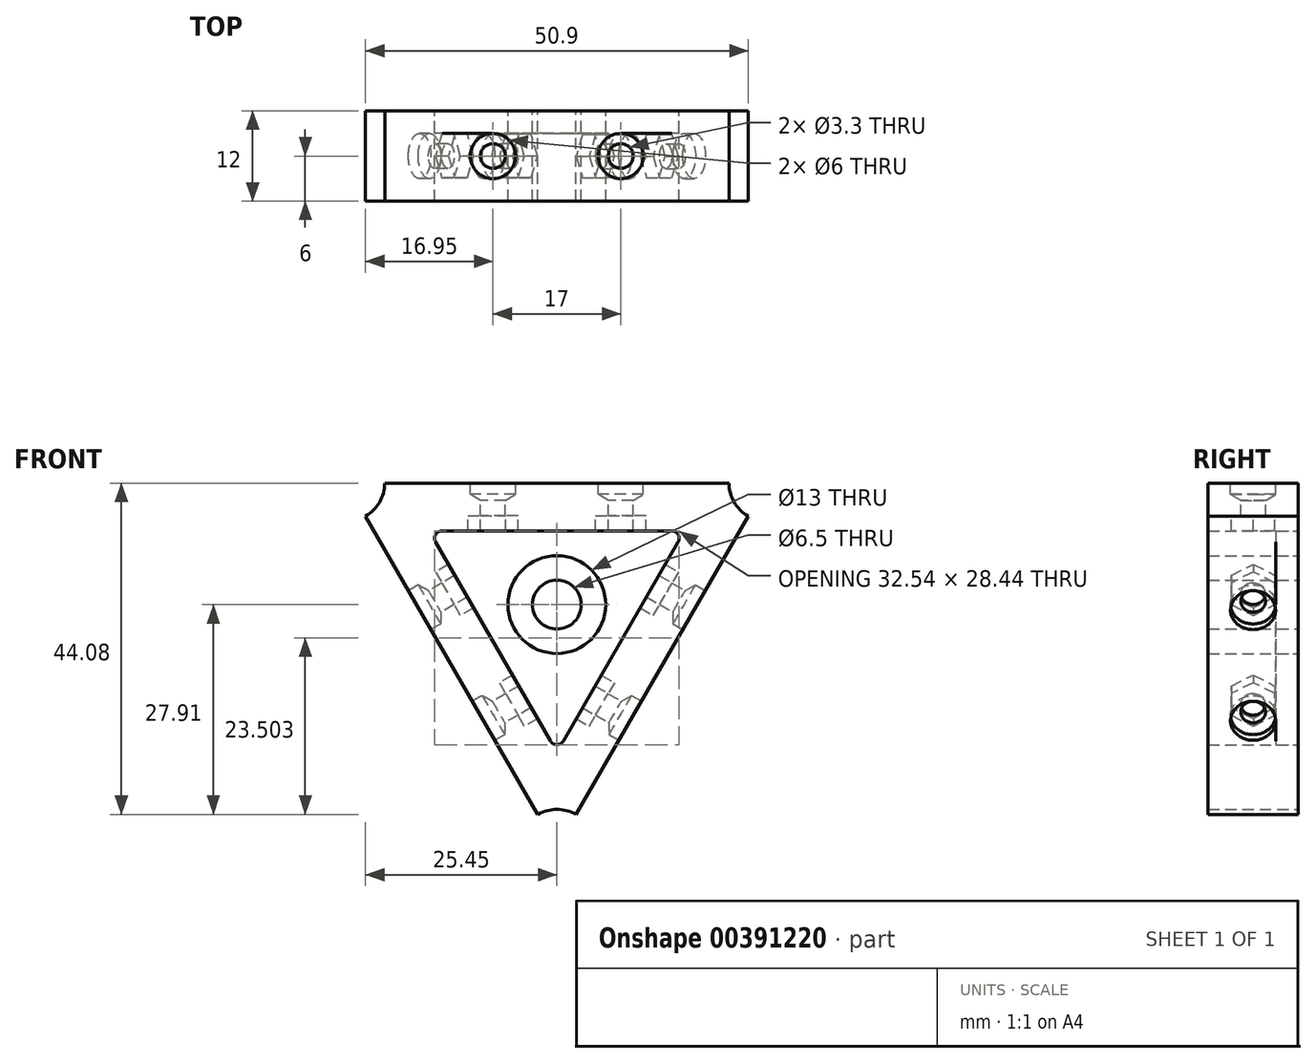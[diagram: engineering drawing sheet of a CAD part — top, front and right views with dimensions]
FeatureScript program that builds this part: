
annotation { "Feature Type Name" : "Feature", "Feature Type Description" : "" }
export const myFeature = defineFeature(function(context is Context, id is Id, definition is map)
    precondition{}
    {
        {
            var Q0;
            Q0=qCreatedBy(makeId("Front.planeOp"),FACE);
            var sketch = newSketch(context, id + "F0", { "sketchPlane" : qUnion([Q0])});
            skCircle(sketch, "E0.cCircle", {"center": v(0, 0) * mm, "radius": 9.81 * mm, "construction": true});
            skLineSegment(sketch, "E0.0", {"start": v(16.13, 8.31) * mm, "end": v(0.87, -18.13) * mm});
            skLineSegment(sketch, "E0.1", {"start": v(-0.87, -18.13) * mm, "end": v(-16.13, 8.31) * mm});
            skLineSegment(sketch, "E0.2", {"start": v(-15.27, 9.81) * mm, "end": v(15.27, 9.81) * mm});
            skPoint(sketch, "E0.0.midPoint", {"position": v(8.5, -4.9) * mm});
            skPoint(sketch, "E1.0.midPoint", {"position": v(14, -8.08) * mm});
            skPoint(sketch, "E2", {"position": v(0, 9.81) * mm});
            skCircle(sketch, "E3", {"center": v(0, 0) * mm, "radius": 3.25 * mm});
            skPoint(sketch, "E4", {"position": v(22.9, 16.17) * mm});
            skPoint(sketch, "E5", {"position": v(-22.9, 16.17) * mm});
            skPoint(sketch, "E6", {"position": v(-25.45, 11.75) * mm});
            skPoint(sketch, "E7", {"position": v(-2.55, -27.91) * mm});
            skPoint(sketch, "E8", {"position": v(2.55, -27.91) * mm});
            skPoint(sketch, "E9", {"position": v(25.45, 11.75) * mm});
            skCircle(sketch, "E10", {"center": v(28, 16.17) * mm, "radius": 5.1 * mm});
            skCircle(sketch, "E11", {"center": v(0, -32.33) * mm, "radius": 5.1 * mm});
            skCircle(sketch, "E12", {"center": v(-28, 16.17) * mm, "radius": 5.1 * mm});
            skLineSegment(sketch, "E13", {"start": v(-22.9, 16.17) * mm, "end": v(22.9, 16.17) * mm});
            skLineSegment(sketch, "E14", {"start": v(25.45, 11.75) * mm, "end": v(2.55, -27.91) * mm});
            skLineSegment(sketch, "E15", {"start": v(-25.45, 11.75) * mm, "end": v(-2.55, -27.91) * mm});
            skPoint(sketch, "E16.visualSharp", {"position": v(17, 9.81) * mm});
            skArc(sketch, "E16.filletArc", {"start": v(16.13, 8.31) * mm, "mid": v(16.13, 9.31) * mm, "end": v(15.27, 9.81) * mm});
            skPoint(sketch, "E17.visualSharp", {"position": v(-17, 9.81) * mm});
            skArc(sketch, "E17.filletArc", {"start": v(-15.27, 9.81) * mm, "mid": v(-16.13, 9.31) * mm, "end": v(-16.13, 8.31) * mm});
            skPoint(sketch, "E18.visualSharp", {"position": v(0, -19.63) * mm});
            skArc(sketch, "E18.filletArc", {"start": v(-0.87, -18.13) * mm, "mid": v(0, -18.63) * mm, "end": v(0.87, -18.13) * mm});
            skCircle(sketch, "E19", {"center": v(0, 0) * mm, "radius": 6.5 * mm});
            skSolve(sketch);
        }
        {
            var Q0;
            Q0=makeQuery(id+"F0.imprint","IMPRINT",FACE,{"disambiguationData":[TD([[makeQuery(id+"F0.imprint","IMPRINT",EDGE,{"derivedFrom":sQuery(id+"F0.wireOp",EDGE,"E0.0")}),1.0]])]});
            var Q1;
            Q1=makeQuery(id+"F0.imprint","IMPRINT",FACE,{"disambiguationData":[TD([[makeQuery(id+"F0.imprint","IMPRINT",EDGE,{"derivedFrom":sQuery(id+"F0.wireOp",EDGE,"E3")}),-1.0]])]});
            extrude(context, id + "F1", {"entities" : qUnion([Q0, Q1]), "depth" : 12 * mm});
        }
        {
            var Q0;
            Q0=makeQuery(id+"F0.imprint","IMPRINT",FACE,{"disambiguationData":[TD([[makeQuery(id+"F0.imprint","IMPRINT",EDGE,{"derivedFrom":sQuery(id+"F0.wireOp",EDGE,"E0.0")}),-1.0]])]});
            extrude(context, id + "F2", {"entities" : qUnion([Q0]), "depth" : 3 * mm});
        }
        {
            var Q0;
            Q0=makeQuery(id+"F1.opExtrude","SWEPT_FACE",FACE,{"disambiguationData":[OSD([sQuery(id+"F0.wireOp",EDGE,"E13")])]});
            var sketch = newSketch(context, id + "F3", { "sketchPlane" : qUnion([Q0])});
            skPoint(sketch, "E20", {"position": v(8.5, -6) * mm});
            skPoint(sketch, "E21", {"position": v(-8.5, -6) * mm});
            skCircle(sketch, "E22.cCircle", {"center": v(-8.5, -6) * mm, "radius": 2.9 * mm, "construction": true});
            skLineSegment(sketch, "E22.0", {"start": v(-5.15, -6) * mm, "end": v(-6.83, -8.9) * mm});
            skLineSegment(sketch, "E22.1", {"start": v(-6.83, -8.9) * mm, "end": v(-10.17, -8.9) * mm});
            skLineSegment(sketch, "E22.2", {"start": v(-10.17, -8.9) * mm, "end": v(-11.85, -6) * mm});
            skLineSegment(sketch, "E22.3", {"start": v(-11.85, -6) * mm, "end": v(-10.17, -3.1) * mm});
            skLineSegment(sketch, "E22.4", {"start": v(-10.17, -3.1) * mm, "end": v(-6.83, -3.1) * mm});
            skLineSegment(sketch, "E22.5", {"start": v(-6.83, -3.1) * mm, "end": v(-5.15, -6) * mm});
            skPoint(sketch, "E22.0.midPoint", {"position": v(-5.99, -7.45) * mm});
            skCircle(sketch, "E23.cCircle", {"center": v(8.5, -6) * mm, "radius": 2.9 * mm, "construction": true});
            skLineSegment(sketch, "E23.0", {"start": v(11.85, -6) * mm, "end": v(10.17, -8.9) * mm});
            skLineSegment(sketch, "E23.1", {"start": v(10.17, -8.9) * mm, "end": v(6.83, -8.9) * mm});
            skLineSegment(sketch, "E23.2", {"start": v(6.83, -8.9) * mm, "end": v(5.15, -6) * mm});
            skLineSegment(sketch, "E23.3", {"start": v(5.15, -6) * mm, "end": v(6.83, -3.1) * mm});
            skLineSegment(sketch, "E23.4", {"start": v(6.83, -3.1) * mm, "end": v(10.17, -3.1) * mm});
            skLineSegment(sketch, "E23.5", {"start": v(10.17, -3.1) * mm, "end": v(11.85, -6) * mm});
            skPoint(sketch, "E23.0.midPoint", {"position": v(11.01, -7.45) * mm});
            skSolve(sketch);
        }
        {
            var Q0;
            Q0 = qSketchRegion(id + "F3", true);
            extrude(context, id + "F4", {"entities" : qUnion([Q0]), "operationType" : NewBodyOperationType.REMOVE, "oppositeDirection" : true, "depth" : 8 * mm, "hasSecondDirection" : true, "secondDirectionOppositeDirection" : true, "secondDirectionDepth" : 4.35 * mm});
        }
        {
            var Q0;
            Q0=sQuery(id+"F3.wireOp",VERTEX,"E20");
            var Q1;
            Q1=sQuery(id+"F3.wireOp",VERTEX,"E21");
            var Q2;
            Q2=makeQuery(id+"F1.opExtrude","SWEPT_BODY",BODY,{"disambiguationData":[OSD([sQuery(id+"F0.wireOp",EDGE,"E0.0"),sQuery(id+"F0.wireOp",EDGE,"E0.1"),sQuery(id+"F0.wireOp",EDGE,"E0.2"),sQuery(id+"F0.wireOp",EDGE,"E10"),sQuery(id+"F0.wireOp",EDGE,"E11"),sQuery(id+"F0.wireOp",EDGE,"E12"),sQuery(id+"F0.wireOp",EDGE,"E13"),sQuery(id+"F0.wireOp",EDGE,"E14"),sQuery(id+"F0.wireOp",EDGE,"E15"),sQuery(id+"F0.wireOp",EDGE,"E16.filletArc"),sQuery(id+"F0.wireOp",EDGE,"E17.filletArc"),sQuery(id+"F0.wireOp",EDGE,"E18.filletArc")])]});
            hole(context, id + "F5", {"style" : HoleStyle.SIMPLE, "endStyle" : HoleEndStyle.BLIND, "standardTappedOrClearance" : lookupTablePath({ "standard" : "ISO", "fit" : "Normal", "size" : "M3", "type" : "Clearance" }), "standardBlindInLast" : lookupTablePath({ "fit" : "Standard", "standard" : "ISO", "size" : "M3", "type" : "Clearance" }), "holeDiameter" : 3.3 * mm, "holeDepth" : 8 * mm, "tappedDepth" : 12 * mm, "tapClearance" : 3, "locations" : qUnion([Q0, Q1]), "scope" : qUnion([Q2])});
        }
        {
            var Q0;
            Q0=sQuery(id+"F3.wireOp",VERTEX,"E20");
            var Q1;
            Q1=sQuery(id+"F3.wireOp",VERTEX,"E21");
            var Q2;
            Q2=makeQuery(id+"F1.opExtrude","SWEPT_BODY",BODY,{"disambiguationData":[OSD([sQuery(id+"F0.wireOp",EDGE,"E0.0"),sQuery(id+"F0.wireOp",EDGE,"E0.1"),sQuery(id+"F0.wireOp",EDGE,"E0.2"),sQuery(id+"F0.wireOp",EDGE,"E10"),sQuery(id+"F0.wireOp",EDGE,"E11"),sQuery(id+"F0.wireOp",EDGE,"E12"),sQuery(id+"F0.wireOp",EDGE,"E13"),sQuery(id+"F0.wireOp",EDGE,"E14"),sQuery(id+"F0.wireOp",EDGE,"E15"),sQuery(id+"F0.wireOp",EDGE,"E16.filletArc"),sQuery(id+"F0.wireOp",EDGE,"E17.filletArc"),sQuery(id+"F0.wireOp",EDGE,"E18.filletArc")])]});
            hole(context, id + "F6", {"style" : HoleStyle.SIMPLE, "endStyle" : HoleEndStyle.BLIND, "holeDiameter" : 6 * mm, "holeDepth" : 1.5 * mm, "tappedDepth" : 12 * mm, "tapClearance" : 3, "locations" : qUnion([Q0, Q1]), "scope" : qUnion([Q2])});
        }
        {
            var Q0;
            Q0=makeQuery(id+"F1.opExtrude","SWEPT_FACE",FACE,{"disambiguationData":[OSD([sQuery(id+"F0.wireOp",EDGE,"E15")])]});
            var sketch = newSketch(context, id + "F7", { "sketchPlane" : qUnion([Q0])});
            skPoint(sketch, "E24", {"position": v(6, -8.5) * mm});
            skPoint(sketch, "E25", {"position": v(6, 8.5) * mm});
            skCircle(sketch, "E26.cCircle", {"center": v(6, 8.5) * mm, "radius": 2.9 * mm, "construction": true});
            skLineSegment(sketch, "E26.0", {"start": v(6, 5.15) * mm, "end": v(3.1, 6.83) * mm});
            skLineSegment(sketch, "E26.1", {"start": v(3.1, 6.83) * mm, "end": v(3.1, 10.17) * mm});
            skLineSegment(sketch, "E26.2", {"start": v(3.1, 10.17) * mm, "end": v(6, 11.85) * mm});
            skLineSegment(sketch, "E26.3", {"start": v(6, 11.85) * mm, "end": v(8.9, 10.17) * mm});
            skLineSegment(sketch, "E26.4", {"start": v(8.9, 10.17) * mm, "end": v(8.9, 6.83) * mm});
            skLineSegment(sketch, "E26.5", {"start": v(8.9, 6.83) * mm, "end": v(6, 5.15) * mm});
            skPoint(sketch, "E26.0.midPoint", {"position": v(4.55, 5.99) * mm});
            skCircle(sketch, "E27.cCircle", {"center": v(6, -8.5) * mm, "radius": 2.9 * mm, "construction": true});
            skLineSegment(sketch, "E27.0", {"start": v(6, -11.85) * mm, "end": v(3.1, -10.17) * mm});
            skLineSegment(sketch, "E27.1", {"start": v(3.1, -10.17) * mm, "end": v(3.1, -6.83) * mm});
            skLineSegment(sketch, "E27.2", {"start": v(3.1, -6.83) * mm, "end": v(6, -5.15) * mm});
            skLineSegment(sketch, "E27.3", {"start": v(6, -5.15) * mm, "end": v(8.9, -6.83) * mm});
            skLineSegment(sketch, "E27.4", {"start": v(8.9, -6.83) * mm, "end": v(8.9, -10.17) * mm});
            skLineSegment(sketch, "E27.5", {"start": v(8.9, -10.17) * mm, "end": v(6, -11.85) * mm});
            skPoint(sketch, "E27.0.midPoint", {"position": v(4.55, -11.01) * mm});
            skSolve(sketch);
        }
        {
            var Q0;
            Q0=makeQuery(id+"F7.imprint","IMPRINT",FACE,{"disambiguationData":[TD([[makeQuery(id+"F7.imprint","IMPRINT",EDGE,{"derivedFrom":sQuery(id+"F7.wireOp",EDGE,"E26.0")}),-1.0]])]});
            var Q1;
            Q1=makeQuery(id+"F7.imprint","IMPRINT",FACE,{"disambiguationData":[TD([[makeQuery(id+"F7.imprint","IMPRINT",EDGE,{"derivedFrom":sQuery(id+"F7.wireOp",EDGE,"E27.0")}),-1.0]])]});
            extrude(context, id + "F8", {"entities" : qUnion([Q0, Q1]), "operationType" : NewBodyOperationType.REMOVE, "oppositeDirection" : true, "depth" : 8 * mm, "hasSecondDirection" : true, "secondDirectionOppositeDirection" : true, "secondDirectionDepth" : 4.35 * mm});
        }
        {
            var Q0;
            Q0=sQuery(id+"F7.wireOp",VERTEX,"E26.cCircle.center");
            var Q1;
            Q1=sQuery(id+"F7.wireOp",VERTEX,"E27.cCircle.center");
            var Q2;
            Q2=makeQuery(id+"F1.opExtrude","SWEPT_BODY",BODY,{"disambiguationData":[OSD([sQuery(id+"F0.wireOp",EDGE,"E0.0"),sQuery(id+"F0.wireOp",EDGE,"E0.1"),sQuery(id+"F0.wireOp",EDGE,"E0.2"),sQuery(id+"F0.wireOp",EDGE,"E10"),sQuery(id+"F0.wireOp",EDGE,"E11"),sQuery(id+"F0.wireOp",EDGE,"E12"),sQuery(id+"F0.wireOp",EDGE,"E13"),sQuery(id+"F0.wireOp",EDGE,"E14"),sQuery(id+"F0.wireOp",EDGE,"E15"),sQuery(id+"F0.wireOp",EDGE,"E16.filletArc"),sQuery(id+"F0.wireOp",EDGE,"E17.filletArc"),sQuery(id+"F0.wireOp",EDGE,"E18.filletArc")])]});
            hole(context, id + "F9", {"style" : HoleStyle.SIMPLE, "endStyle" : HoleEndStyle.BLIND, "holeDiameter" : 6 * mm, "holeDepth" : 1.5 * mm, "tappedDepth" : 12 * mm, "tapClearance" : 3, "locations" : qUnion([Q0, Q1]), "scope" : qUnion([Q2])});
        }
        {
            var Q0;
            Q0=sQuery(id+"F7.wireOp",VERTEX,"E25");
            var Q1;
            Q1=sQuery(id+"F7.wireOp",VERTEX,"E24");
            var Q2;
            Q2=makeQuery(id+"F1.opExtrude","SWEPT_BODY",BODY,{"disambiguationData":[OSD([sQuery(id+"F0.wireOp",EDGE,"E0.0"),sQuery(id+"F0.wireOp",EDGE,"E0.1"),sQuery(id+"F0.wireOp",EDGE,"E0.2"),sQuery(id+"F0.wireOp",EDGE,"E10"),sQuery(id+"F0.wireOp",EDGE,"E11"),sQuery(id+"F0.wireOp",EDGE,"E12"),sQuery(id+"F0.wireOp",EDGE,"E13"),sQuery(id+"F0.wireOp",EDGE,"E14"),sQuery(id+"F0.wireOp",EDGE,"E15"),sQuery(id+"F0.wireOp",EDGE,"E16.filletArc"),sQuery(id+"F0.wireOp",EDGE,"E17.filletArc"),sQuery(id+"F0.wireOp",EDGE,"E18.filletArc")])]});
            hole(context, id + "F10", {"style" : HoleStyle.SIMPLE, "endStyle" : HoleEndStyle.BLIND, "standardTappedOrClearance" : lookupTablePath({ "standard" : "ISO", "fit" : "Normal", "size" : "M3", "type" : "Clearance" }), "standardBlindInLast" : lookupTablePath({ "fit" : "Standard", "standard" : "ISO", "size" : "M3", "type" : "Clearance" }), "holeDiameter" : 3.3 * mm, "holeDepth" : 8 * mm, "tappedDepth" : 12 * mm, "tapClearance" : 3, "locations" : qUnion([Q0, Q1]), "scope" : qUnion([Q2])});
        }
        {
            var Q0;
            Q0=makeQuery(id+"F1.opExtrude","SWEPT_FACE",FACE,{"disambiguationData":[OSD([sQuery(id+"F0.wireOp",EDGE,"E14")])]});
            var sketch = newSketch(context, id + "F11", { "sketchPlane" : qUnion([Q0])});
            skPoint(sketch, "E28", {"position": v(-6, 8.5) * mm});
            skPoint(sketch, "E29", {"position": v(-6, -8.5) * mm});
            skCircle(sketch, "E30.cCircle", {"center": v(-6, -8.5) * mm, "radius": 2.9 * mm, "construction": true});
            skLineSegment(sketch, "E30.0", {"start": v(-6, -5.15) * mm, "end": v(-3.1, -6.83) * mm});
            skLineSegment(sketch, "E30.1", {"start": v(-3.1, -6.83) * mm, "end": v(-3.1, -10.17) * mm});
            skLineSegment(sketch, "E30.2", {"start": v(-3.1, -10.17) * mm, "end": v(-6, -11.85) * mm});
            skLineSegment(sketch, "E30.3", {"start": v(-6, -11.85) * mm, "end": v(-8.9, -10.17) * mm});
            skLineSegment(sketch, "E30.4", {"start": v(-8.9, -10.17) * mm, "end": v(-8.9, -6.83) * mm});
            skLineSegment(sketch, "E30.5", {"start": v(-8.9, -6.83) * mm, "end": v(-6, -5.15) * mm});
            skPoint(sketch, "E30.0.midPoint", {"position": v(-4.55, -5.99) * mm});
            skCircle(sketch, "E31.cCircle", {"center": v(-6, 8.5) * mm, "radius": 2.9 * mm, "construction": true});
            skLineSegment(sketch, "E31.0", {"start": v(-3.1, 10.17) * mm, "end": v(-3.1, 6.83) * mm});
            skLineSegment(sketch, "E31.1", {"start": v(-3.1, 6.83) * mm, "end": v(-6, 5.15) * mm});
            skLineSegment(sketch, "E31.2", {"start": v(-6, 5.15) * mm, "end": v(-8.9, 6.83) * mm});
            skLineSegment(sketch, "E31.3", {"start": v(-8.9, 6.83) * mm, "end": v(-8.9, 10.17) * mm});
            skLineSegment(sketch, "E31.4", {"start": v(-8.9, 10.17) * mm, "end": v(-6, 11.85) * mm});
            skLineSegment(sketch, "E31.5", {"start": v(-6, 11.85) * mm, "end": v(-3.1, 10.17) * mm});
            skPoint(sketch, "E31.0.midPoint", {"position": v(-3.1, 8.5) * mm});
            skSolve(sketch);
        }
        {
            var Q0;
            Q0 = qSketchRegion(id + "F11", true);
            extrude(context, id + "F12", {"entities" : qUnion([Q0]), "operationType" : NewBodyOperationType.REMOVE, "oppositeDirection" : true, "depth" : 8 * mm, "hasSecondDirection" : true, "secondDirectionOppositeDirection" : true, "secondDirectionDepth" : 4.35 * mm});
        }
        {
            var Q0;
            Q0=sQuery(id+"F11.wireOp",VERTEX,"E30.cCircle.center");
            var Q1;
            Q1=sQuery(id+"F11.wireOp",VERTEX,"E28");
            var Q2;
            Q2=makeQuery(id+"F1.opExtrude","SWEPT_BODY",BODY,{"disambiguationData":[OSD([sQuery(id+"F0.wireOp",EDGE,"E0.0"),sQuery(id+"F0.wireOp",EDGE,"E0.1"),sQuery(id+"F0.wireOp",EDGE,"E0.2"),sQuery(id+"F0.wireOp",EDGE,"E10"),sQuery(id+"F0.wireOp",EDGE,"E11"),sQuery(id+"F0.wireOp",EDGE,"E12"),sQuery(id+"F0.wireOp",EDGE,"E13"),sQuery(id+"F0.wireOp",EDGE,"E14"),sQuery(id+"F0.wireOp",EDGE,"E15"),sQuery(id+"F0.wireOp",EDGE,"E16.filletArc"),sQuery(id+"F0.wireOp",EDGE,"E17.filletArc"),sQuery(id+"F0.wireOp",EDGE,"E18.filletArc")])]});
            hole(context, id + "F13", {"style" : HoleStyle.SIMPLE, "endStyle" : HoleEndStyle.BLIND, "standardTappedOrClearance" : lookupTablePath({ "standard" : "ISO", "fit" : "Normal", "size" : "M3", "type" : "Clearance" }), "standardBlindInLast" : lookupTablePath({ "fit" : "Standard", "standard" : "ISO", "size" : "M3", "type" : "Clearance" }), "holeDiameter" : 3.3 * mm, "holeDepth" : 8 * mm, "tappedDepth" : 12 * mm, "tapClearance" : 3, "locations" : qUnion([Q0, Q1]), "scope" : qUnion([Q2])});
        }
        {
            var Q0;
            Q0=sQuery(id+"F11.wireOp",VERTEX,"E29");
            var Q1;
            Q1=sQuery(id+"F11.wireOp",VERTEX,"E28");
            var Q2;
            Q2=makeQuery(id+"F1.opExtrude","SWEPT_BODY",BODY,{"disambiguationData":[OSD([sQuery(id+"F0.wireOp",EDGE,"E0.0"),sQuery(id+"F0.wireOp",EDGE,"E0.1"),sQuery(id+"F0.wireOp",EDGE,"E0.2"),sQuery(id+"F0.wireOp",EDGE,"E10"),sQuery(id+"F0.wireOp",EDGE,"E11"),sQuery(id+"F0.wireOp",EDGE,"E12"),sQuery(id+"F0.wireOp",EDGE,"E13"),sQuery(id+"F0.wireOp",EDGE,"E14"),sQuery(id+"F0.wireOp",EDGE,"E15"),sQuery(id+"F0.wireOp",EDGE,"E16.filletArc"),sQuery(id+"F0.wireOp",EDGE,"E17.filletArc"),sQuery(id+"F0.wireOp",EDGE,"E18.filletArc")])]});
            hole(context, id + "F14", {"style" : HoleStyle.SIMPLE, "endStyle" : HoleEndStyle.BLIND, "holeDiameter" : 6 * mm, "holeDepth" : 1.5 * mm, "tappedDepth" : 12 * mm, "tapClearance" : 3, "locations" : qUnion([Q0, Q1]), "scope" : qUnion([Q2])});
        }
    });
